# Revit family: Facade_60_Curtain_Wall_E13_Custom
name_source: partatom
category: Windows
revit_build: Autodesk Revit 2014 (Build: 20130308_1515(x64)
units: mm (PartAtom-declared; Revit-internal decimal feet)

## types (1)
- F60-E13-Custom
    100mm Mullion = Yes
    160mm Mullion = No
    190mm Mullion = No
    DG Gasket Thickness = 12 mm  [stored 0.0393701 ft]
    Default Sill Height = 0 mm  [stored 0 ft]
    Description = Curtain Wall, E13
    Frame Bottom Gap = 30 mm
    Frame Thickness = 102 mm
    Glazing Bottom Gap = 70 mm
    Glazing Side Gap = 40 mm  [stored 0.131234 ft]
    Glazing Top Gap = 40 mm  [stored 0.131234 ft]
    Half Expansion Break = No
    Intruderprufe Insulated LowE SHGC Value = 0
    Intruderprufe Insulated LowE U Value = 0
    Intruderprufe Insulated SHGC Value = 0
    Intruderprufe Insulated U Value = 0
    Intruderprufe LowE SHGC Value = 0
    Intruderprufe LowE U Value = 0
    Intruderprufe SHGC Value = 0
    Intruderprufe U Value = 0
    Jamb Width = 60 mm  [stored 0.19685 ft]
    Limit Door Height Max = 18149 mm
    Limit Door Height Min = 1049 mm
    Limit Door Width Max = 3080 mm
    Limit Door Width Min = 380 mm
    Limit Panel Height Max = 6000 mm
    Limit Panel Height Min = 300 mm
    Limit Panel Width Max = 3000 mm  [stored 9.84252 ft]
    Limit Panel Width Min = 300 mm
    Manufacturer = Crealco
    Max System DG Unit Thickness = 25 mm  [stored 0.082021 ft]
    Model = Facade 60
    Mullion Configuration = 1 mm  [stored 0.00328084 ft]
    Quarter Expansion Break = Yes
    Sill Height = 85 mm
    Thermal Break Material = Plastic, Opaque Black
    URL = http://www.crealco.co.za
    Wall Closure = By host

note: [stored X ft] marks values corroborated as IEEE doubles in the binary element streams (Revit-internal decimal feet)

## geometry (parser evidence)
native form markers: Sweep x16
no freeform markers — native parametric forms only
